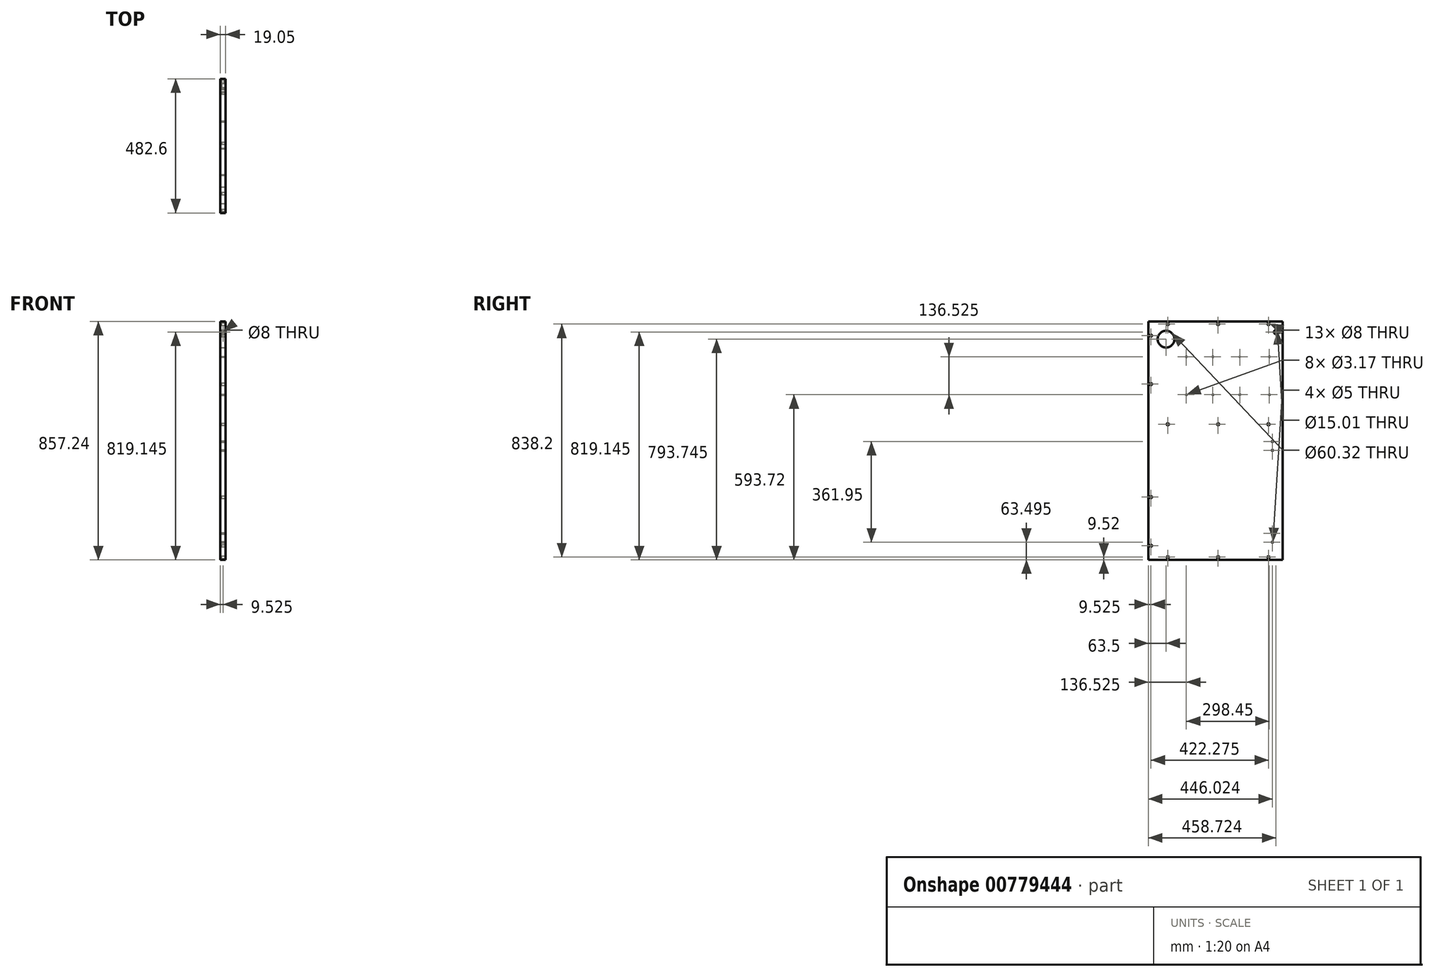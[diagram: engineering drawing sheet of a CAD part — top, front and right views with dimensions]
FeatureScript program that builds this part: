
annotation { "Feature Type Name" : "Feature", "Feature Type Description" : "" }
export const myFeature = defineFeature(function(context is Context, id is Id, definition is map)
    precondition{}
    {
        {
            var Q0;
            Q0=qCreatedBy(makeId("Right.planeOp"),FACE);
            var sketch = newSketch(context, id + "F0", { "sketchPlane" : qUnion([Q0])});
            skLineSegment(sketch, "E0.bottom", {"start": v(241.3, 428.63) * mm, "end": v(-241.3, 428.63) * mm});
            skLineSegment(sketch, "E0.top", {"start": v(241.3, -428.63) * mm, "end": v(-241.3, -428.63) * mm});
            skLineSegment(sketch, "E0.left", {"start": v(241.3, 428.63) * mm, "end": v(241.3, -428.63) * mm});
            skLineSegment(sketch, "E0.right", {"start": v(-241.3, 428.63) * mm, "end": v(-241.3, -428.63) * mm});
            skPoint(sketch, "E0.middle", {"position": v(0, 0) * mm});
            skSolve(sketch);
        }
        {
            var Q0;
            Q0=makeQuery(id+"F0.imprint","IMPRINT",FACE,{"disambiguationData":[TD([[makeQuery(id+"F0.imprint","IMPRINT",EDGE,{"derivedFrom":sQuery(id+"F0.wireOp",EDGE,"E0.bottom")}),1.0]])]});
            extrude(context, id + "F1", {"entities" : qUnion([Q0]), "depth" : 19.05 * mm, "offsetDistance" : 25.4 * mm});
        }
        {
            var Q0;
            Q0=makeQuery(id+"F1.opExtrude","CAP_FACE",FACE,{"disambiguationData":[OSD([sQuery(id+"F0.wireOp",EDGE,"E0.bottom"),sQuery(id+"F0.wireOp",EDGE,"E0.top"),sQuery(id+"F0.wireOp",EDGE,"E0.left"),sQuery(id+"F0.wireOp",EDGE,"E0.right")])],"isStart":false});
            var sketch = newSketch(context, id + "F2", { "sketchPlane" : qUnion([Q0])});
            skLineSegment(sketch, "E1", {"start": v(-241.3, 428.63) * mm, "end": v(-241.3, 419.1) * mm});
            skLineSegment(sketch, "E2", {"start": v(-241.3, 419.1) * mm, "end": v(-190.5, 419.1) * mm});
            skLineSegment(sketch, "E3", {"start": v(241.3, 428.63) * mm, "end": v(241.3, 419.1) * mm});
            skLineSegment(sketch, "E4", {"start": v(241.3, 419.1) * mm, "end": v(171.45, 419.1) * mm});
            skLineSegment(sketch, "E5", {"start": v(-241.3, 419.1) * mm, "end": v(-9.53, 419.1) * mm});
            skPoint(sketch, "E6", {"position": v(-190.5, 419.1) * mm});
            skPoint(sketch, "E7", {"position": v(-9.53, 419.1) * mm});
            skPoint(sketch, "E8", {"position": v(171.45, 419.1) * mm});
            skLineSegment(sketch, "E9", {"start": v(-241.3, -428.63) * mm, "end": v(-241.3, -419.1) * mm});
            skLineSegment(sketch, "E10", {"start": v(-241.3, -419.1) * mm, "end": v(-190.5, -419.1) * mm});
            skLineSegment(sketch, "E11", {"start": v(-241.3, -419.1) * mm, "end": v(-9.53, -419.1) * mm});
            skLineSegment(sketch, "E12", {"start": v(241.3, -428.63) * mm, "end": v(241.3, -419.1) * mm});
            skLineSegment(sketch, "E13", {"start": v(241.3, -419.1) * mm, "end": v(171.45, -419.1) * mm});
            skPoint(sketch, "E14", {"position": v(-190.5, -419.1) * mm});
            skPoint(sketch, "E15", {"position": v(-9.53, -419.1) * mm});
            skPoint(sketch, "E16", {"position": v(171.45, -419.1) * mm});
            skLineSegment(sketch, "E17", {"start": v(241.3, 428.63) * mm, "end": v(231.77, 428.63) * mm});
            skLineSegment(sketch, "E18", {"start": v(231.77, 428.63) * mm, "end": v(231.77, 377.83) * mm});
            skLineSegment(sketch, "E19", {"start": v(241.3, -428.63) * mm, "end": v(231.77, -428.63) * mm});
            skLineSegment(sketch, "E20", {"start": v(231.77, -428.63) * mm, "end": v(231.77, -377.83) * mm});
            skLineSegment(sketch, "E21", {"start": v(241.3, 0) * mm, "end": v(231.77, 0) * mm});
            skLineSegment(sketch, "E22", {"start": v(231.77, 0) * mm, "end": v(231.77, 203.2) * mm});
            skLineSegment(sketch, "E23", {"start": v(231.77, 0) * mm, "end": v(231.77, -203.2) * mm});
            skPoint(sketch, "E24", {"position": v(231.77, 203.2) * mm});
            skPoint(sketch, "E25", {"position": v(231.77, -203.2) * mm});
            skPoint(sketch, "E26", {"position": v(231.77, 377.83) * mm});
            skPoint(sketch, "E27", {"position": v(231.77, -377.83) * mm});
            skSolve(sketch);
        }
        {
            var Q0;
            Q0=sQuery(id+"F2.wireOp",VERTEX,"E6");
            var Q1;
            Q1=sQuery(id+"F2.wireOp",VERTEX,"E7");
            var Q2;
            Q2=sQuery(id+"F2.wireOp",VERTEX,"E8");
            var Q3;
            Q3=sQuery(id+"F2.wireOp",VERTEX,"E26");
            var Q4;
            Q4=sQuery(id+"F2.wireOp",VERTEX,"E24");
            var Q5;
            Q5=sQuery(id+"F2.wireOp",VERTEX,"E25");
            var Q6;
            Q6=sQuery(id+"F2.wireOp",VERTEX,"E27");
            var Q7;
            Q7=sQuery(id+"F2.wireOp",VERTEX,"E16");
            var Q8;
            Q8=sQuery(id+"F2.wireOp",VERTEX,"E15");
            var Q9;
            Q9=sQuery(id+"F2.wireOp",VERTEX,"E14");
            var Q10;
            Q10=makeQuery(id+"F1.opExtrude","SWEPT_BODY",BODY,{"disambiguationData":[OSD([sQuery(id+"F0.wireOp",EDGE,"E0.bottom"),sQuery(id+"F0.wireOp",EDGE,"E0.top"),sQuery(id+"F0.wireOp",EDGE,"E0.left"),sQuery(id+"F0.wireOp",EDGE,"E0.right")])]});
            hole(context, id + "F3", {"style" : HoleStyle.SIMPLE, "endStyle" : HoleEndStyle.BLIND, "holeDiameter" : 8 * mm, "majorDiameter" : 6.35 * mm, "holeDepth" : 14.22 * mm, "isTappedThrough" : true, "tappedDepth" : 12.7 * mm, "tapClearance" : 3, "startFromSketch" : true, "locations" : qUnion([Q0, Q1, Q2, Q3, Q4, Q5, Q6, Q7, Q8, Q9]), "scope" : qUnion([Q10])});
        }
        {
            var Q0;
            Q0=makeQuery(id+"F1.opExtrude","CAP_FACE",FACE,{"disambiguationData":[OSD([sQuery(id+"F0.wireOp",EDGE,"E0.bottom"),sQuery(id+"F0.wireOp",EDGE,"E0.top"),sQuery(id+"F0.wireOp",EDGE,"E0.left"),sQuery(id+"F0.wireOp",EDGE,"E0.right")])],"isStart":false});
            var sketch = newSketch(context, id + "F4", { "sketchPlane" : qUnion([Q0])});
            skLineSegment(sketch, "E28", {"start": v(-241.3, 428.63) * mm, "end": v(-241.3, 390.53) * mm});
            skLineSegment(sketch, "E29", {"start": v(-241.3, 390.53) * mm, "end": v(-217.42, 390.53) * mm});
            skPoint(sketch, "E30", {"position": v(-217.42, 390.53) * mm});
            skSolve(sketch);
        }
        {
            var Q0;
            Q0=sQuery(id+"F4.wireOp",VERTEX,"E29.end");
            var Q1;
            Q1=makeQuery(id+"F1.opExtrude","SWEPT_BODY",BODY,{"disambiguationData":[OSD([sQuery(id+"F0.wireOp",EDGE,"E0.bottom"),sQuery(id+"F0.wireOp",EDGE,"E0.top"),sQuery(id+"F0.wireOp",EDGE,"E0.left"),sQuery(id+"F0.wireOp",EDGE,"E0.right")])]});
            hole(context, id + "F5", {"style" : HoleStyle.SIMPLE, "endStyle" : HoleEndStyle.BLIND, "holeDiameter" : 15 * mm, "majorDiameter" : 6.35 * mm, "holeDepth" : 14.22 * mm, "isTappedThrough" : true, "tappedDepth" : 12.7 * mm, "tapClearance" : 3, "startFromSketch" : true, "locations" : qUnion([Q0]), "scope" : qUnion([Q1])});
        }
        {
            var Q0;
            Q0=makeQuery(id+"F1.opExtrude","SWEPT_FACE",FACE,{"disambiguationData":[OSD([sQuery(id+"F0.wireOp",EDGE,"E0.right")])]});
            var sketch = newSketch(context, id + "F6", { "sketchPlane" : qUnion([Q0])});
            skLineSegment(sketch, "E31", {"start": v(9.53, 428.63) * mm, "end": v(9.53, 390.53) * mm});
            skPoint(sketch, "E32", {"position": v(9.53, 390.53) * mm});
            skSolve(sketch);
        }
        {
            var Q0;
            Q0=sQuery(id+"F6.wireOp",VERTEX,"E32");
            var Q1;
            Q1=makeQuery(id+"F1.opExtrude","SWEPT_BODY",BODY,{"disambiguationData":[OSD([sQuery(id+"F0.wireOp",EDGE,"E0.bottom"),sQuery(id+"F0.wireOp",EDGE,"E0.top"),sQuery(id+"F0.wireOp",EDGE,"E0.left"),sQuery(id+"F0.wireOp",EDGE,"E0.right")])]});
            hole(context, id + "F7", {"style" : HoleStyle.SIMPLE, "endStyle" : HoleEndStyle.BLIND, "holeDiameter" : 8 * mm, "majorDiameter" : 6.35 * mm, "holeDepth" : 25.4 * mm, "isTappedThrough" : true, "tappedDepth" : 12.7 * mm, "tapClearance" : 3, "startFromSketch" : true, "locations" : qUnion([Q0]), "scope" : qUnion([Q1])});
        }
        {
            var Q0;
            Q0=makeQuery(id+"F1.opExtrude","CAP_FACE",FACE,{"disambiguationData":[OSD([sQuery(id+"F0.wireOp",EDGE,"E0.bottom"),sQuery(id+"F0.wireOp",EDGE,"E0.top"),sQuery(id+"F0.wireOp",EDGE,"E0.left"),sQuery(id+"F0.wireOp",EDGE,"E0.right")])],"isStart":false});
            var sketch = newSketch(context, id + "F8", { "sketchPlane" : qUnion([Q0])});
            skLineSegment(sketch, "E33", {"start": v(-241.3, 428.63) * mm, "end": v(-241.3, 301.63) * mm});
            skLineSegment(sketch, "E34", {"start": v(-241.3, 301.63) * mm, "end": v(-193.68, 301.63) * mm});
            skLineSegment(sketch, "E35", {"start": v(-193.68, 301.63) * mm, "end": v(-241.3, 301.63) * mm});
            skLineSegment(sketch, "E36", {"start": v(-241.3, 301.63) * mm, "end": v(-87.38, 301.63) * mm});
            skLineSegment(sketch, "E37", {"start": v(-241.3, 301.63) * mm, "end": v(9.52, 301.63) * mm});
            skLineSegment(sketch, "E38", {"start": v(-241.3, 301.63) * mm, "end": v(104.77, 301.63) * mm});
            skPoint(sketch, "E39", {"position": v(-193.68, 301.63) * mm});
            skPoint(sketch, "E40", {"position": v(-87.38, 301.63) * mm});
            skPoint(sketch, "E41", {"position": v(104.77, 301.63) * mm});
            skLineSegment(sketch, "E42", {"start": v(-241.3, 428.63) * mm, "end": v(-241.3, 269.88) * mm});
            skLineSegment(sketch, "E43", {"start": v(-241.3, 269.88) * mm, "end": v(-241.3, 60.33) * mm});
            skLineSegment(sketch, "E44", {"start": v(-241.3, 428.63) * mm, "end": v(-241.3, 352.43) * mm});
            skPoint(sketch, "E45.endSnap0", {"position": v(-241.3, 349.25) * mm});
            skLineSegment(sketch, "E46", {"start": v(-241.3, 352.43) * mm, "end": v(-241.3, 349.25) * mm});
            skLineSegment(sketch, "E47", {"start": v(-241.3, 349.25) * mm, "end": v(-241.3, 273.05) * mm});
            skLineSegment(sketch, "E48", {"start": v(-241.3, 273.05) * mm, "end": v(-241.3, 269.88) * mm});
            skLineSegment(sketch, "E49", {"start": v(-241.3, 349.25) * mm, "end": v(-241.3, 346.08) * mm});
            skLineSegment(sketch, "E50.bottom", {"start": v(-241.3, 346.08) * mm, "end": v(165.1, 346.08) * mm});
            skLineSegment(sketch, "E50.top", {"start": v(-241.3, 327.03) * mm, "end": v(165.1, 327.03) * mm});
            skLineSegment(sketch, "E50.left", {"start": v(-241.3, 346.08) * mm, "end": v(-241.3, 327.03) * mm});
            skLineSegment(sketch, "E50.right", {"start": v(165.1, 346.08) * mm, "end": v(165.1, 327.03) * mm});
            skLineSegment(sketch, "E51.top", {"start": v(-241.3, 276.23) * mm, "end": v(165.1, 276.23) * mm});
            skLineSegment(sketch, "E51.left", {"start": v(-241.3, 327.03) * mm, "end": v(-241.3, 276.23) * mm});
            skLineSegment(sketch, "E51.right", {"start": v(165.1, 327.03) * mm, "end": v(165.1, 276.23) * mm});
            skLineSegment(sketch, "E52", {"start": v(-241.3, 165.1) * mm, "end": v(-193.68, 165.1) * mm});
            skLineSegment(sketch, "E53", {"start": v(-241.3, 165.1) * mm, "end": v(-87.38, 165.1) * mm});
            skLineSegment(sketch, "E54", {"start": v(-241.3, 165.1) * mm, "end": v(9.52, 165.1) * mm});
            skLineSegment(sketch, "E55", {"start": v(-241.3, 165.1) * mm, "end": v(104.77, 165.1) * mm});
            skPoint(sketch, "E56", {"position": v(-193.68, 165.1) * mm});
            skPoint(sketch, "E57", {"position": v(-87.38, 165.1) * mm});
            skPoint(sketch, "E58", {"position": v(9.52, 165.1) * mm});
            skPoint(sketch, "E59", {"position": v(104.77, 165.1) * mm});
            skLineSegment(sketch, "E60", {"start": v(-241.3, 60.33) * mm, "end": v(-241.3, 57.15) * mm});
            skLineSegment(sketch, "E61", {"start": v(-241.3, 57.15) * mm, "end": v(-241.3, -428.63) * mm});
            skLineSegment(sketch, "E62", {"start": v(-241.3, 57.15) * mm, "end": v(-241.3, -19.05) * mm});
            skLineSegment(sketch, "E63", {"start": v(-241.3, -19.05) * mm, "end": v(-204.72, -19.05) * mm});
            skLineSegment(sketch, "E64", {"start": v(-204.72, -19.05) * mm, "end": v(-204.72, -3.17) * mm});
            skLineSegment(sketch, "E65", {"start": v(-204.72, -3.17) * mm, "end": v(-204.72, -34.92) * mm});
            skPoint(sketch, "E65.endSnap0", {"position": v(-204.72, -11.11) * mm});
            skPoint(sketch, "E66", {"position": v(-204.72, -3.17) * mm});
            skPoint(sketch, "E67", {"position": v(-204.72, -34.92) * mm});
            skLineSegment(sketch, "E68", {"start": v(-241.3, 57.15) * mm, "end": v(-241.3, -349.25) * mm});
            skLineSegment(sketch, "E69", {"start": v(-241.3, -349.25) * mm, "end": v(-204.72, -349.25) * mm});
            skLineSegment(sketch, "E70", {"start": v(-204.72, -349.25) * mm, "end": v(-204.72, -333.38) * mm});
            skLineSegment(sketch, "E71", {"start": v(-204.72, -333.38) * mm, "end": v(-204.72, -365.12) * mm});
            skPoint(sketch, "E72", {"position": v(-204.72, -333.38) * mm});
            skPoint(sketch, "E73", {"position": v(-204.72, -365.12) * mm});
            skLineSegment(sketch, "E74", {"start": v(-241.3, 58.74) * mm, "end": v(-190.5, 58.74) * mm});
            skLineSegment(sketch, "E75", {"start": v(-190.5, 58.74) * mm, "end": v(171.45, 58.74) * mm});
            skLineSegment(sketch, "E76", {"start": v(-241.3, 58.74) * mm, "end": v(-9.53, 58.74) * mm});
            skPoint(sketch, "E77", {"position": v(-190.5, 58.74) * mm});
            skPoint(sketch, "E78", {"position": v(-9.53, 58.74) * mm});
            skPoint(sketch, "E79", {"position": v(171.45, 58.74) * mm});
            skSolve(sketch);
        }
        {
            var Q0;
            Q0=sQuery(id+"F8.wireOp",VERTEX,"E39");
            var Q1;
            Q1=sQuery(id+"F8.wireOp",VERTEX,"E40");
            var Q2;
            Q2=sQuery(id+"F8.wireOp",VERTEX,"E41");
            var Q3;
            Q3=sQuery(id+"F8.wireOp",VERTEX,"E59");
            var Q4;
            Q4=sQuery(id+"F8.wireOp",VERTEX,"E58");
            var Q5;
            Q5=sQuery(id+"F8.wireOp",VERTEX,"E57");
            var Q6;
            Q6=sQuery(id+"F8.wireOp",VERTEX,"E37.end");
            var Q7;
            Q7=sQuery(id+"F8.wireOp",VERTEX,"E56");
            var Q8;
            Q8=makeQuery(id+"F1.opExtrude","SWEPT_BODY",BODY,{"disambiguationData":[OSD([sQuery(id+"F0.wireOp",EDGE,"E0.bottom"),sQuery(id+"F0.wireOp",EDGE,"E0.top"),sQuery(id+"F0.wireOp",EDGE,"E0.left"),sQuery(id+"F0.wireOp",EDGE,"E0.right")])]});
            hole(context, id + "F9", {"style" : HoleStyle.SIMPLE, "endStyle" : HoleEndStyle.BLIND, "holeDiameter" : 3.17 * mm, "majorDiameter" : 6.35 * mm, "holeDepth" : 14.22 * mm, "isTappedThrough" : true, "tappedDepth" : 12.7 * mm, "tapClearance" : 3, "startFromSketch" : true, "locations" : qUnion([Q0, Q1, Q2, Q3, Q4, Q5, Q6, Q7]), "scope" : qUnion([Q8])});
        }
        {
            var Q0;
            Q0=sQuery(id+"F8.wireOp",VERTEX,"E66");
            var Q1;
            Q1=sQuery(id+"F8.wireOp",VERTEX,"E67");
            var Q2;
            Q2=sQuery(id+"F8.wireOp",VERTEX,"E72");
            var Q3;
            Q3=sQuery(id+"F8.wireOp",VERTEX,"E73");
            var Q4;
            Q4=makeQuery(id+"F1.opExtrude","SWEPT_BODY",BODY,{"disambiguationData":[OSD([sQuery(id+"F0.wireOp",EDGE,"E0.bottom"),sQuery(id+"F0.wireOp",EDGE,"E0.top"),sQuery(id+"F0.wireOp",EDGE,"E0.left"),sQuery(id+"F0.wireOp",EDGE,"E0.right")])]});
            hole(context, id + "F10", {"style" : HoleStyle.SIMPLE, "endStyle" : HoleEndStyle.BLIND, "holeDiameter" : 5 * mm, "majorDiameter" : 6.35 * mm, "holeDepth" : 14.22 * mm, "isTappedThrough" : true, "tappedDepth" : 12.7 * mm, "tapClearance" : 3, "startFromSketch" : true, "locations" : qUnion([Q0, Q1, Q2, Q3]), "scope" : qUnion([Q4])});
        }
        {
            var Q0;
            Q0=makeQuery(id+"F1.opExtrude","CAP_FACE",FACE,{"disambiguationData":[OSD([sQuery(id+"F0.wireOp",EDGE,"E0.bottom"),sQuery(id+"F0.wireOp",EDGE,"E0.top"),sQuery(id+"F0.wireOp",EDGE,"E0.left"),sQuery(id+"F0.wireOp",EDGE,"E0.right")])],"isStart":false});
            var sketch = newSketch(context, id + "F11", { "sketchPlane" : qUnion([Q0])});
            skLineSegment(sketch, "E80", {"start": v(241.3, 428.63) * mm, "end": v(177.8, 428.63) * mm});
            skLineSegment(sketch, "E81", {"start": v(177.8, 428.63) * mm, "end": v(177.8, 365.13) * mm});
            skCircle(sketch, "E82", {"center": v(177.8, 365.13) * mm, "radius": 30.16 * mm});
            skSolve(sketch);
        }
        {
            var Q0;
            Q0=makeQuery(id+"F11.imprint","IMPRINT",FACE,{"disambiguationData":[TD([[makeQuery(id+"F11.imprint","IMPRINT",EDGE,{"derivedFrom":sQuery(id+"F11.wireOp",EDGE,"E82")}),1.0]])]});
            extrude(context, id + "F12", {"entities" : qUnion([Q0]), "operationType" : NewBodyOperationType.REMOVE, "oppositeDirection" : true, "depth" : 25.4 * mm, "offsetDistance" : 25.4 * mm});
        }
        {
            var Q0;
            Q0=sQuery(id+"F8.wireOp",VERTEX,"E77");
            var Q1;
            Q1=sQuery(id+"F8.wireOp",VERTEX,"E78");
            var Q2;
            Q2=sQuery(id+"F8.wireOp",VERTEX,"E79");
            var Q3;
            Q3=makeQuery(id+"F1.opExtrude","SWEPT_BODY",BODY,{"disambiguationData":[OSD([sQuery(id+"F0.wireOp",EDGE,"E0.bottom"),sQuery(id+"F0.wireOp",EDGE,"E0.top"),sQuery(id+"F0.wireOp",EDGE,"E0.left"),sQuery(id+"F0.wireOp",EDGE,"E0.right")])]});
            hole(context, id + "F13", {"style" : HoleStyle.SIMPLE, "endStyle" : HoleEndStyle.BLIND, "holeDiameter" : 8 * mm, "majorDiameter" : 6.35 * mm, "holeDepth" : 14.22 * mm, "isTappedThrough" : true, "tappedDepth" : 12.7 * mm, "tapClearance" : 3, "startFromSketch" : true, "locations" : qUnion([Q0, Q1, Q2]), "scope" : qUnion([Q3])});
        }
        {
            var Q0;
            Q0=makeQuery(id+"F1.opExtrude","SWEPT_BODY",BODY,{"disambiguationData":[OSD([sQuery(id+"F0.wireOp",EDGE,"E0.bottom"),sQuery(id+"F0.wireOp",EDGE,"E0.top"),sQuery(id+"F0.wireOp",EDGE,"E0.left"),sQuery(id+"F0.wireOp",EDGE,"E0.right")])]});
            var Q1;
            Q1=makeQuery(id+"F1.opExtrude","SWEPT_FACE",FACE,{"disambiguationData":[OSD([sQuery(id+"F0.wireOp",EDGE,"E0.left")])]});
            mirror(context, id + "F14", {"entities" : qUnion([Q0]), "mirrorPlane" : qUnion([Q1])});
        }
        {
            var Q0;
            Q0=makeQuery(id+"F1.opExtrude","SWEPT_BODY",BODY,{"disambiguationData":[OSD([sQuery(id+"F0.wireOp",EDGE,"E0.bottom"),sQuery(id+"F0.wireOp",EDGE,"E0.top"),sQuery(id+"F0.wireOp",EDGE,"E0.left"),sQuery(id+"F0.wireOp",EDGE,"E0.right")])]});
            deleteBodies(context, id + "F15", {"entities" : qUnion([Q0])});
        }
    });
